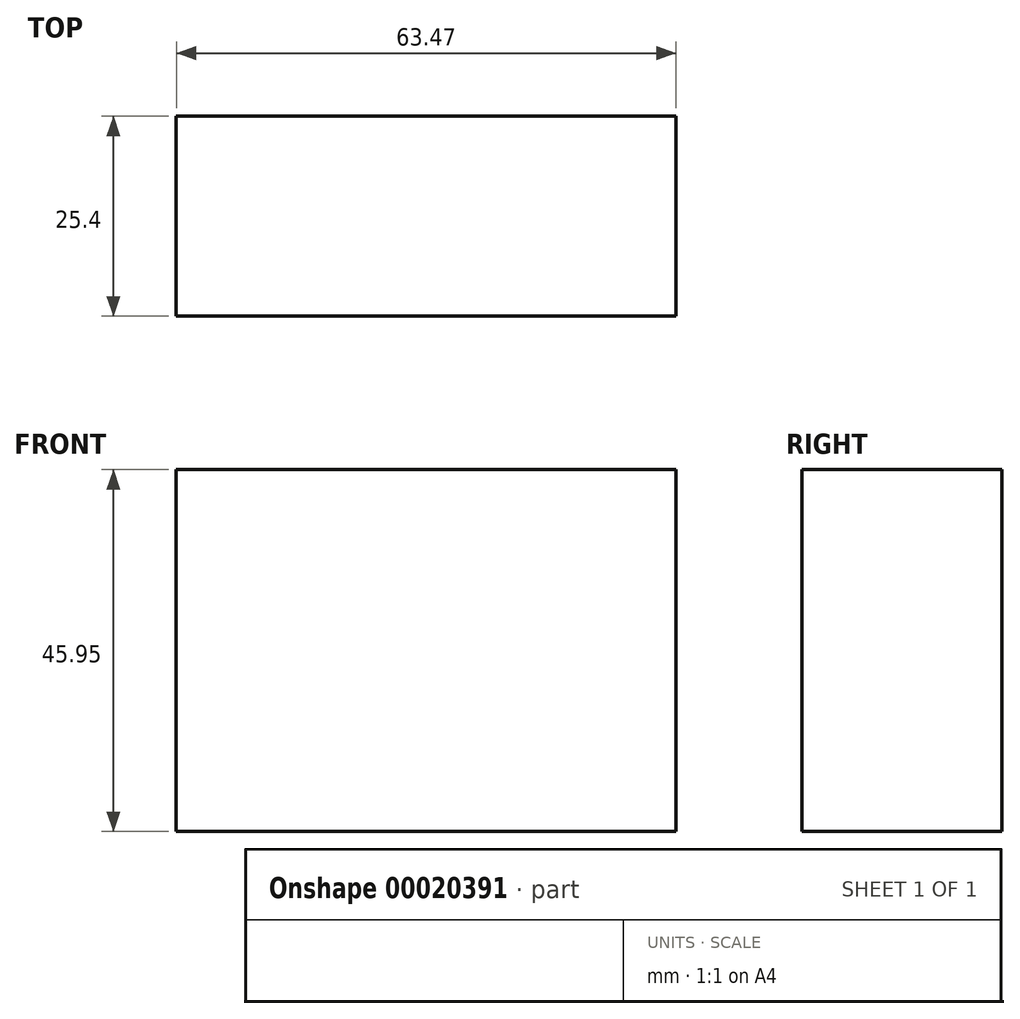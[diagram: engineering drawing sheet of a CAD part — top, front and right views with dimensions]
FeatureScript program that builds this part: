
annotation { "Feature Type Name" : "Feature", "Feature Type Description" : "" }
export const myFeature = defineFeature(function(context is Context, id is Id, definition is map)
    precondition{}
    {
        {
            var Q0;
            Q0=qCreatedBy(makeId("Front.planeOp"),FACE);
            var sketch = newSketch(context, id + "F0", { "sketchPlane" : qUnion([Q0])});
            skLineSegment(sketch, "E0.bottom", {"start": v(-24.35, 22.71) * mm, "end": v(39.12, 22.71) * mm});
            skLineSegment(sketch, "E0.top", {"start": v(-24.35, -23.24) * mm, "end": v(39.12, -23.24) * mm});
            skLineSegment(sketch, "E0.left", {"start": v(-24.35, 22.71) * mm, "end": v(-24.35, -23.24) * mm});
            skLineSegment(sketch, "E0.right", {"start": v(39.12, 22.71) * mm, "end": v(39.12, -23.24) * mm});
            skSolve(sketch);
        }
        {
            var Q0;
            Q0 = qSketchRegion(id + "F0", true);
            extrude(context, id + "F1", {"entities" : qUnion([Q0]), "endBound" : BoundingType.SYMMETRIC, "depth" : 25.4 * mm});
        }
    });
